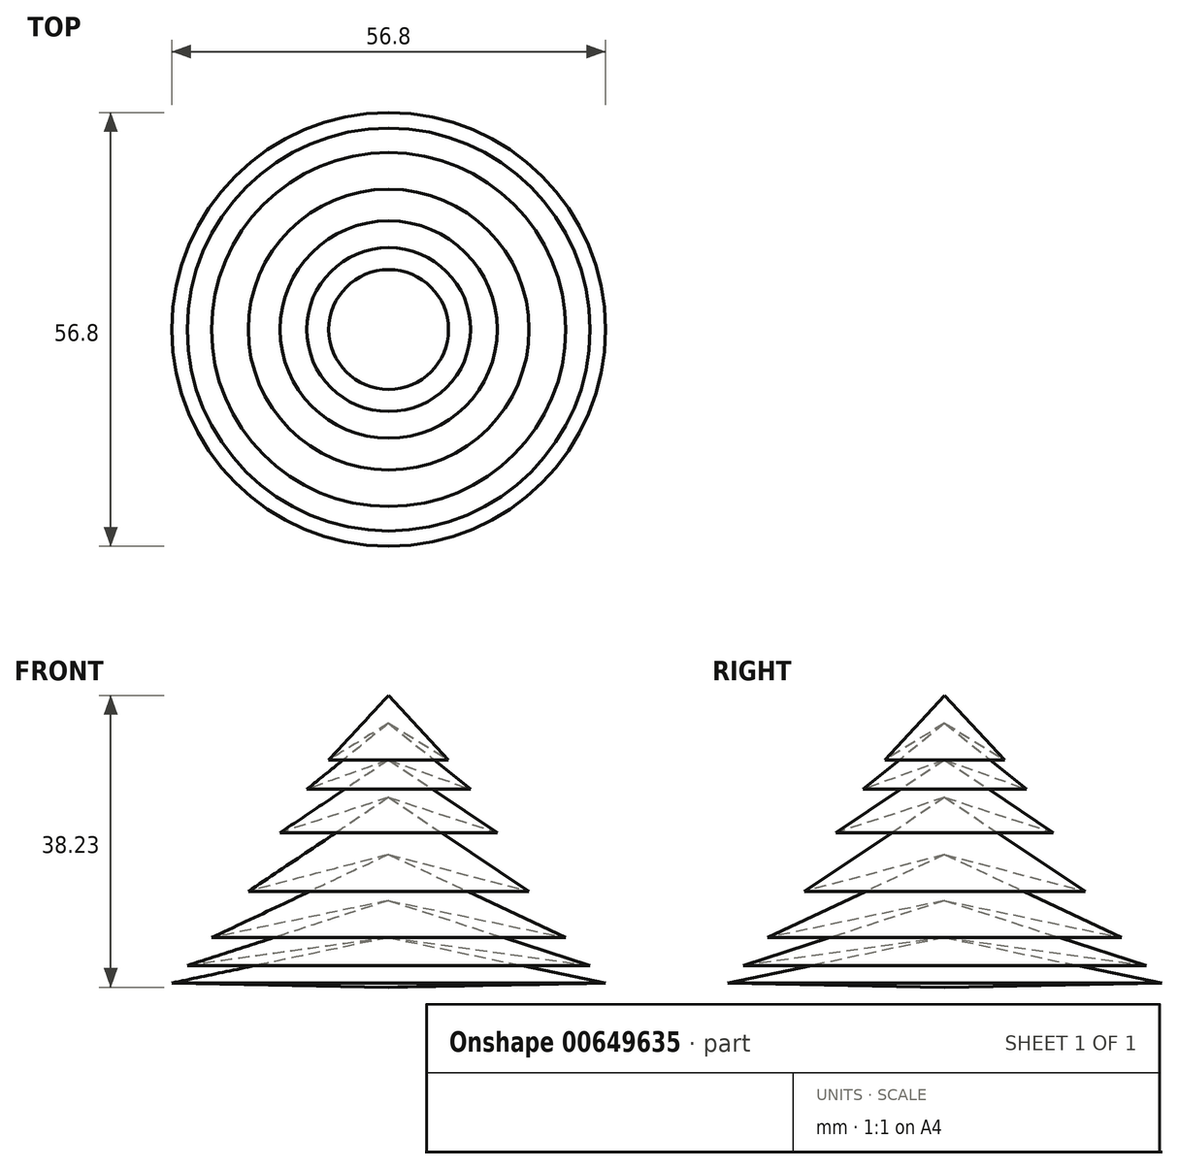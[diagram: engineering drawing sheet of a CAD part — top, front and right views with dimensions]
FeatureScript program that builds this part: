
annotation { "Feature Type Name" : "Feature", "Feature Type Description" : "" }
export const myFeature = defineFeature(function(context is Context, id is Id, definition is map)
    precondition{}
    {
        {
            var Q0;
            Q0=qCreatedBy(makeId("Front.planeOp"),FACE);
            var sketch = newSketch(context, id + "F0", { "sketchPlane" : qUnion([Q0])});
            skLineSegment(sketch, "E0", {"start": v(0, 0) * mm, "end": v(0, 38.23) * mm});
            skLineSegment(sketch, "E1", {"start": v(0, 38.23) * mm, "end": v(-7.84, 29.77) * mm});
            skLineSegment(sketch, "E2", {"start": v(-7.84, 29.77) * mm, "end": v(0, 34.57) * mm});
            skLineSegment(sketch, "E3", {"start": v(-7.84, 24.86) * mm, "end": v(0, 29.77) * mm});
            skLineSegment(sketch, "E4", {"start": v(0, 29.77) * mm, "end": v(-14.22, 20.23) * mm});
            skLineSegment(sketch, "E5", {"start": v(-14.22, 20.23) * mm, "end": v(0, 24.86) * mm});
            skLineSegment(sketch, "E6", {"start": v(0, 24.86) * mm, "end": v(-18.38, 12.54) * mm});
            skLineSegment(sketch, "E7", {"start": v(-18.38, 12.54) * mm, "end": v(0, 17.4) * mm});
            skLineSegment(sketch, "E8", {"start": v(0, 17.4) * mm, "end": v(-23.18, 6.5) * mm});
            skLineSegment(sketch, "E9", {"start": v(-23.18, 6.5) * mm, "end": v(0, 11.36) * mm});
            skLineSegment(sketch, "E10", {"start": v(0, 11.36) * mm, "end": v(-26.37, 2.85) * mm});
            skLineSegment(sketch, "E11", {"start": v(-26.37, 2.85) * mm, "end": v(0, 6.5) * mm});
            skLineSegment(sketch, "E12", {"start": v(0, 6.5) * mm, "end": v(-28.4, 0.55) * mm});
            skLineSegment(sketch, "E13", {"start": v(-28.4, 0.55) * mm, "end": v(0, 0) * mm});
            skLineSegment(sketch, "E14", {"start": v(0, 34.57) * mm, "end": v(-10.72, 25.92) * mm});
            skLineSegment(sketch, "E15", {"start": v(-10.72, 25.92) * mm, "end": v(0, 29.77) * mm});
            skSolve(sketch);
        }
        {
            var Q0;
            {var subQ0=sQuery(id+"F0.wireOp",EDGE,"E6");Q0=makeQuery(id+"F0.imprint","IMPRINT",FACE,{"disambiguationData":[TD([[makeQuery(id+"F0.imprint","IMPRINT",EDGE,{"derivedFrom":subQ0}),1.0]])]});}
            var Q1;
            {var subQ0=sQuery(id+"F0.wireOp",EDGE,"E4");Q1=makeQuery(id+"F0.imprint","IMPRINT",FACE,{"disambiguationData":[TD([[makeQuery(id+"F0.imprint","IMPRINT",EDGE,{"derivedFrom":subQ0}),1.0]])]});}
            var Q2;
            {var subQ0=sQuery(id+"F0.wireOp",EDGE,"E1");Q2=makeQuery(id+"F0.imprint","IMPRINT",FACE,{"disambiguationData":[TD([[makeQuery(id+"F0.imprint","IMPRINT",EDGE,{"derivedFrom":subQ0}),1.0]])]});}
            var Q3;
            {var subQ0=sQuery(id+"F0.wireOp",EDGE,"E14");Q3=makeQuery(id+"F0.imprint","IMPRINT",FACE,{"disambiguationData":[TD([[makeQuery(id+"F0.imprint","IMPRINT",EDGE,{"derivedFrom":subQ0}),1.0]])]});}
            var Q4;
            {var subQ0=sQuery(id+"F0.wireOp",EDGE,"E8");Q4=makeQuery(id+"F0.imprint","IMPRINT",FACE,{"disambiguationData":[TD([[makeQuery(id+"F0.imprint","IMPRINT",EDGE,{"derivedFrom":subQ0}),1.0]])]});}
            var Q5;
            {var subQ0=sQuery(id+"F0.wireOp",EDGE,"E10");Q5=makeQuery(id+"F0.imprint","IMPRINT",FACE,{"disambiguationData":[TD([[makeQuery(id+"F0.imprint","IMPRINT",EDGE,{"derivedFrom":subQ0}),1.0]])]});}
            var Q6;
            {var subQ2=sQuery(id+"F0.wireOp",EDGE,"E12");Q6=makeQuery(id+"F0.imprint","IMPRINT",FACE,{"disambiguationData":[TD([[makeQuery(id+"F0.imprint","IMPRINT",EDGE,{"derivedFrom":subQ2}),1.0]])]});}
            var Q7;
            Q7=sQuery(id+"F0.wireOp",EDGE,"E0");
            revolve(context, id + "F1", {"entities" : qUnion([Q0, Q1, Q2, Q3, Q4, Q5, Q6]), "axis" : qUnion([Q7]), "revolveType" : RevolveType.FULL});
        }
    });
